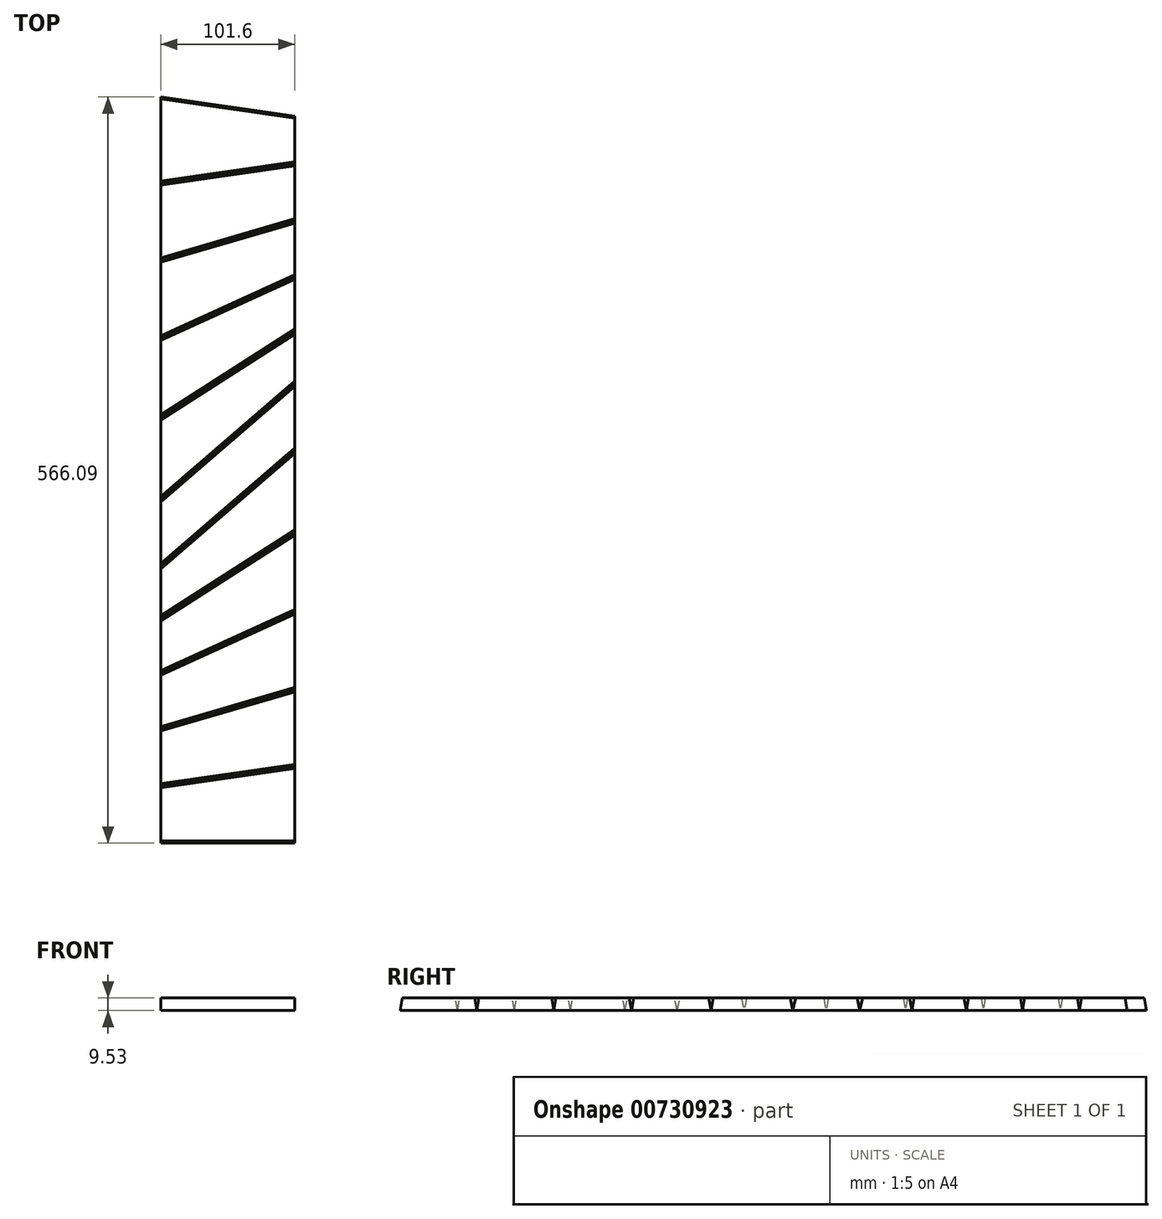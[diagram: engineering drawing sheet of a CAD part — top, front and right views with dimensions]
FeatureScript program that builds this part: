
annotation { "Feature Type Name" : "Feature", "Feature Type Description" : "" }
export const myFeature = defineFeature(function(context is Context, id is Id, definition is map)
    precondition{}
    {
        {
            assignVariable(context, id + "F0", {"name" : "Chamfer", "anyValue" : 9.25});
        }
        {
            var Q0;
            Q0=qCreatedBy(makeId("Top.planeOp"),FACE);
            var sketch = newSketch(context, id + "F1", { "sketchPlane" : qUnion([Q0])});
            skLineSegment(sketch, "E0.bottom", {"start": v(-50.8, 279.4) * mm, "end": v(50.8, 279.4) * mm, "construction": true});
            skLineSegment(sketch, "E0.top", {"start": v(-50.8, -279.4) * mm, "end": v(50.8, -279.4) * mm});
            skLineSegment(sketch, "E0.left", {"start": v(-50.8, 279.4) * mm, "end": v(-50.8, -279.4) * mm});
            skLineSegment(sketch, "E0.right", {"start": v(50.8, 279.4) * mm, "end": v(50.8, -279.4) * mm, "construction": true});
            skPoint(sketch, "E0.middle", {"position": v(0, 0) * mm});
            skLineSegment(sketch, "E1", {"start": v(0, 279.4) * mm, "end": v(0, -279.4) * mm, "construction": true});
            skLineSegment(sketch, "E2", {"start": v(-50.8, 0) * mm, "end": v(50.8, 0) * mm, "construction": true});
            skLineSegment(sketch, "E3", {"start": v(50.8, 235.89) * mm, "end": v(-50.8, 221.31) * mm});
            skLineSegment(sketch, "E4", {"start": v(50.8, 192.68) * mm, "end": v(-50.8, 162.92) * mm});
            skLineSegment(sketch, "E5", {"start": v(50.8, 150.14) * mm, "end": v(-50.8, 103.86) * mm});
            skLineSegment(sketch, "E6", {"start": v(50.8, 108.75) * mm, "end": v(-50.8, 43.65) * mm});
            skPoint(sketch, "E7", {"position": v(0, 177.8) * mm});
            skPoint(sketch, "E8", {"position": v(0, 127) * mm});
            skPoint(sketch, "E9", {"position": v(0, 76.2) * mm});
            skPoint(sketch, "E10", {"position": v(0, 228.6) * mm});
            skLineSegment(sketch, "E11", {"start": v(50.8, 69.27) * mm, "end": v(-50.8, -18.47) * mm});
            skPoint(sketch, "E12", {"position": v(0, 25.4) * mm});
            skLineSegment(sketch, "E13.1.1", {"start": v(-50.8, -69.27) * mm, "end": v(50.8, 18.47) * mm});
            skLineSegment(sketch, "E13.1.2", {"start": v(-50.8, -108.75) * mm, "end": v(50.8, -43.65) * mm});
            skLineSegment(sketch, "E13.1.3", {"start": v(-50.8, -150.14) * mm, "end": v(50.8, -103.86) * mm});
            skLineSegment(sketch, "E13.1.4", {"start": v(-50.8, -192.68) * mm, "end": v(50.8, -162.92) * mm});
            skLineSegment(sketch, "E13.1.5", {"start": v(-50.8, -235.89) * mm, "end": v(50.8, -221.31) * mm});
            skLineSegment(sketch, "E14", {"start": v(50.8, 272.11) * mm, "end": v(-50.8, 286.69) * mm});
            skLineSegment(sketch, "E15", {"start": v(-50.8, 286.69) * mm, "end": v(-50.8, 279.4) * mm});
            skLineSegment(sketch, "E16", {"start": v(50.8, 272.11) * mm, "end": v(50.8, -279.4) * mm});
            skSolve(sketch);
        }
        {
            var Q0;
            {var subQ1=sQuery(id+"F1.wireOp",EDGE,"E3");Q0=makeQuery(id+"F1.imprint","IMPRINT",FACE,{"disambiguationData":[TD([[makeQuery(id+"F1.imprint","IMPRINT",EDGE,{"derivedFrom":subQ1}),-1.0]])]});}
            extrude(context, id + "F2", {"entities" : qUnion([Q0]), "depth" : 9.52 * mm, "offsetDistance" : 25.4 * mm});
        }
        {
            var Q0;
            {var subQ0=sQuery(id+"F1.wireOp",EDGE,"E3");Q0=makeQuery(id+"F1.imprint","IMPRINT",FACE,{"disambiguationData":[TD([[makeQuery(id+"F1.imprint","IMPRINT",EDGE,{"derivedFrom":subQ0}),1.0]])]});}
            extrude(context, id + "F3", {"entities" : qUnion([Q0]), "depth" : 9.52 * mm, "offsetDistance" : 25.4 * mm});
        }
        {
            var Q0;
            {var subQ0=sQuery(id+"F1.wireOp",EDGE,"E4");Q0=makeQuery(id+"F1.imprint","IMPRINT",FACE,{"disambiguationData":[TD([[makeQuery(id+"F1.imprint","IMPRINT",EDGE,{"derivedFrom":subQ0}),1.0]])]});}
            extrude(context, id + "F4", {"entities" : qUnion([Q0]), "depth" : 9.52 * mm, "offsetDistance" : 25.4 * mm});
        }
        {
            var Q0;
            {var subQ0=sQuery(id+"F1.wireOp",EDGE,"E5");Q0=makeQuery(id+"F1.imprint","IMPRINT",FACE,{"disambiguationData":[TD([[makeQuery(id+"F1.imprint","IMPRINT",EDGE,{"derivedFrom":subQ0}),1.0]])]});}
            extrude(context, id + "F5", {"entities" : qUnion([Q0]), "depth" : 9.52 * mm, "offsetDistance" : 25.4 * mm});
        }
        {
            var Q0;
            {var subQ0=sQuery(id+"F1.wireOp",EDGE,"E6");Q0=makeQuery(id+"F1.imprint","IMPRINT",FACE,{"disambiguationData":[TD([[makeQuery(id+"F1.imprint","IMPRINT",EDGE,{"derivedFrom":subQ0}),1.0]])]});}
            extrude(context, id + "F6", {"entities" : qUnion([Q0]), "depth" : 9.52 * mm, "offsetDistance" : 25.4 * mm});
        }
        {
            var Q0;
            {var subQ0=sQuery(id+"F1.wireOp",EDGE,"E11");Q0=makeQuery(id+"F1.imprint","IMPRINT",FACE,{"disambiguationData":[TD([[makeQuery(id+"F1.imprint","IMPRINT",EDGE,{"derivedFrom":subQ0}),1.0]])]});}
            extrude(context, id + "F7", {"entities" : qUnion([Q0]), "depth" : 9.52 * mm, "offsetDistance" : 25.4 * mm});
        }
        {
            var Q0;
            {var subQ0=sQuery(id+"F1.wireOp",EDGE,"E13.1.1");Q0=makeQuery(id+"F1.imprint","IMPRINT",FACE,{"disambiguationData":[TD([[makeQuery(id+"F1.imprint","IMPRINT",EDGE,{"derivedFrom":subQ0}),-1.0]])]});}
            extrude(context, id + "F8", {"entities" : qUnion([Q0]), "depth" : 9.52 * mm, "offsetDistance" : 25.4 * mm});
        }
        {
            var Q0;
            {var subQ0=sQuery(id+"F1.wireOp",EDGE,"E13.1.2");Q0=makeQuery(id+"F1.imprint","IMPRINT",FACE,{"disambiguationData":[TD([[makeQuery(id+"F1.imprint","IMPRINT",EDGE,{"derivedFrom":subQ0}),-1.0]])]});}
            extrude(context, id + "F9", {"entities" : qUnion([Q0]), "depth" : 9.52 * mm, "offsetDistance" : 25.4 * mm});
        }
        {
            var Q0;
            {var subQ0=sQuery(id+"F1.wireOp",EDGE,"E13.1.3");Q0=makeQuery(id+"F1.imprint","IMPRINT",FACE,{"disambiguationData":[TD([[makeQuery(id+"F1.imprint","IMPRINT",EDGE,{"derivedFrom":subQ0}),-1.0]])]});}
            extrude(context, id + "F10", {"entities" : qUnion([Q0]), "depth" : 9.52 * mm, "offsetDistance" : 25.4 * mm});
        }
        {
            var Q0;
            {var subQ0=sQuery(id+"F1.wireOp",EDGE,"E13.1.4");Q0=makeQuery(id+"F1.imprint","IMPRINT",FACE,{"disambiguationData":[TD([[makeQuery(id+"F1.imprint","IMPRINT",EDGE,{"derivedFrom":subQ0}),-1.0]])]});}
            extrude(context, id + "F11", {"entities" : qUnion([Q0]), "depth" : 9.52 * mm, "offsetDistance" : 25.4 * mm});
        }
        {
            var Q0;
            {var subQ0=sQuery(id+"F1.wireOp",EDGE,"E0.top");Q0=makeQuery(id+"F1.imprint","IMPRINT",FACE,{"disambiguationData":[TD([[makeQuery(id+"F1.imprint","IMPRINT",EDGE,{"derivedFrom":subQ0}),1.0]])]});}
            extrude(context, id + "F12", {"entities" : qUnion([Q0]), "depth" : 9.52 * mm, "offsetDistance" : 25.4 * mm});
        }
        {
            var Q0;
            Q0=makeQuery(id+"F2.opExtrude","CAP_EDGE",EDGE,{"disambiguationData":[OSD([sQuery(id+"F1.wireOp",EDGE,"E3")])],"isStart":false});
            var Q1;
            Q1=makeQuery(id+"F2.opExtrude","CAP_EDGE",EDGE,{"disambiguationData":[OSD([sQuery(id+"F1.wireOp",EDGE,"E14")])],"isStart":false});
            chamfer(context, id + "F13", {"entities" : qUnion([Q0, Q1]), "chamferType" : ChamferType.OFFSET_ANGLE, "width" : 9.52 * mm, "oppositeDirection" : false, "angle" : (getVariable(context, 'Chamfer')) * degree, "tangentPropagation" : true});
        }
        {
            var Q0;
            Q0=makeQuery(id+"F3.opExtrude","CAP_EDGE",EDGE,{"disambiguationData":[OSD([sQuery(id+"F1.wireOp",EDGE,"E3")])],"isStart":false});
            var Q1;
            Q1=makeQuery(id+"F3.opExtrude","CAP_EDGE",EDGE,{"disambiguationData":[OSD([sQuery(id+"F1.wireOp",EDGE,"E4")])],"isStart":false});
            chamfer(context, id + "F14", {"entities" : qUnion([Q0, Q1]), "chamferType" : ChamferType.OFFSET_ANGLE, "width" : 9.52 * mm, "oppositeDirection" : true, "angle" : (getVariable(context, 'Chamfer')) * degree, "tangentPropagation" : true});
        }
        {
            var Q0;
            Q0=makeQuery(id+"F4.opExtrude","CAP_EDGE",EDGE,{"disambiguationData":[OSD([sQuery(id+"F1.wireOp",EDGE,"E4")])],"isStart":false});
            var Q1;
            Q1=makeQuery(id+"F4.opExtrude","CAP_EDGE",EDGE,{"disambiguationData":[OSD([sQuery(id+"F1.wireOp",EDGE,"E5")])],"isStart":false});
            chamfer(context, id + "F15", {"entities" : qUnion([Q0, Q1]), "chamferType" : ChamferType.OFFSET_ANGLE, "width" : 9.52 * mm, "oppositeDirection" : true, "angle" : (getVariable(context, 'Chamfer')) * degree, "tangentPropagation" : true});
        }
        {
            var Q0;
            Q0=makeQuery(id+"F5.opExtrude","CAP_EDGE",EDGE,{"disambiguationData":[OSD([sQuery(id+"F1.wireOp",EDGE,"E5")])],"isStart":false});
            var Q1;
            Q1=makeQuery(id+"F5.opExtrude","CAP_EDGE",EDGE,{"disambiguationData":[OSD([sQuery(id+"F1.wireOp",EDGE,"E6")])],"isStart":false});
            chamfer(context, id + "F16", {"entities" : qUnion([Q0, Q1]), "chamferType" : ChamferType.OFFSET_ANGLE, "width" : 9.52 * mm, "oppositeDirection" : true, "angle" : (getVariable(context, 'Chamfer')) * degree, "tangentPropagation" : true});
        }
        {
            var Q0;
            Q0=makeQuery(id+"F6.opExtrude","CAP_EDGE",EDGE,{"disambiguationData":[OSD([sQuery(id+"F1.wireOp",EDGE,"E11")])],"isStart":false});
            var Q1;
            Q1=makeQuery(id+"F6.opExtrude","CAP_EDGE",EDGE,{"disambiguationData":[OSD([sQuery(id+"F1.wireOp",EDGE,"E6")])],"isStart":false});
            chamfer(context, id + "F17", {"entities" : qUnion([Q0, Q1]), "chamferType" : ChamferType.OFFSET_ANGLE, "width" : 9.52 * mm, "oppositeDirection" : false, "angle" : (getVariable(context, 'Chamfer')) * degree, "tangentPropagation" : true});
        }
        {
            var Q0;
            Q0=makeQuery(id+"F7.opExtrude","CAP_EDGE",EDGE,{"disambiguationData":[OSD([sQuery(id+"F1.wireOp",EDGE,"E11")])],"isStart":false});
            var Q1;
            Q1=makeQuery(id+"F7.opExtrude","CAP_EDGE",EDGE,{"disambiguationData":[OSD([sQuery(id+"F1.wireOp",EDGE,"E13.1.1")])],"isStart":false});
            chamfer(context, id + "F18", {"entities" : qUnion([Q0, Q1]), "chamferType" : ChamferType.OFFSET_ANGLE, "width" : 9.52 * mm, "oppositeDirection" : true, "angle" : (getVariable(context, 'Chamfer')) * degree, "tangentPropagation" : true});
        }
        {
            var Q0;
            Q0=makeQuery(id+"F8.opExtrude","CAP_EDGE",EDGE,{"disambiguationData":[OSD([sQuery(id+"F1.wireOp",EDGE,"E13.1.1")])],"isStart":false});
            var Q1;
            Q1=makeQuery(id+"F8.opExtrude","CAP_EDGE",EDGE,{"disambiguationData":[OSD([sQuery(id+"F1.wireOp",EDGE,"E13.1.2")])],"isStart":false});
            chamfer(context, id + "F19", {"entities" : qUnion([Q0, Q1]), "chamferType" : ChamferType.OFFSET_ANGLE, "width" : 9.52 * mm, "oppositeDirection" : false, "angle" : (getVariable(context, 'Chamfer')) * degree, "tangentPropagation" : true});
        }
        {
            var Q0;
            Q0=makeQuery(id+"F9.opExtrude","CAP_EDGE",EDGE,{"disambiguationData":[OSD([sQuery(id+"F1.wireOp",EDGE,"E13.1.2")])],"isStart":false});
            var Q1;
            Q1=makeQuery(id+"F9.opExtrude","CAP_EDGE",EDGE,{"disambiguationData":[OSD([sQuery(id+"F1.wireOp",EDGE,"E13.1.3")])],"isStart":false});
            chamfer(context, id + "F20", {"entities" : qUnion([Q0, Q1]), "chamferType" : ChamferType.OFFSET_ANGLE, "width" : 9.52 * mm, "oppositeDirection" : false, "angle" : (getVariable(context, 'Chamfer')) * degree, "tangentPropagation" : true});
        }
        {
            var Q0;
            Q0=makeQuery(id+"F10.opExtrude","CAP_EDGE",EDGE,{"disambiguationData":[OSD([sQuery(id+"F1.wireOp",EDGE,"E13.1.3")])],"isStart":false});
            var Q1;
            Q1=makeQuery(id+"F10.opExtrude","CAP_EDGE",EDGE,{"disambiguationData":[OSD([sQuery(id+"F1.wireOp",EDGE,"E13.1.4")])],"isStart":false});
            chamfer(context, id + "F21", {"entities" : qUnion([Q0, Q1]), "chamferType" : ChamferType.OFFSET_ANGLE, "width" : 9.52 * mm, "oppositeDirection" : false, "angle" : (getVariable(context, 'Chamfer')) * degree, "tangentPropagation" : true});
        }
        {
            var Q0;
            Q0=makeQuery(id+"F11.opExtrude","CAP_EDGE",EDGE,{"disambiguationData":[OSD([sQuery(id+"F1.wireOp",EDGE,"E13.1.4")])],"isStart":false});
            var Q1;
            Q1=makeQuery(id+"F11.opExtrude","CAP_EDGE",EDGE,{"disambiguationData":[OSD([sQuery(id+"F1.wireOp",EDGE,"E13.1.5")])],"isStart":false});
            chamfer(context, id + "F22", {"entities" : qUnion([Q0, Q1]), "chamferType" : ChamferType.OFFSET_ANGLE, "width" : 9.52 * mm, "oppositeDirection" : false, "angle" : (getVariable(context, 'Chamfer')) * degree, "tangentPropagation" : true});
        }
        {
            var Q0;
            Q0=makeQuery(id+"F12.opExtrude","CAP_EDGE",EDGE,{"disambiguationData":[OSD([sQuery(id+"F1.wireOp",EDGE,"E13.1.5")])],"isStart":false});
            var Q1;
            Q1=makeQuery(id+"F12.opExtrude","CAP_EDGE",EDGE,{"disambiguationData":[OSD([sQuery(id+"F1.wireOp",EDGE,"E0.top")])],"isStart":false});
            chamfer(context, id + "F23", {"entities" : qUnion([Q0, Q1]), "chamferType" : ChamferType.OFFSET_ANGLE, "width" : 9.52 * mm, "oppositeDirection" : false, "angle" : (getVariable(context, 'Chamfer')) * degree, "tangentPropagation" : true});
        }
    });
